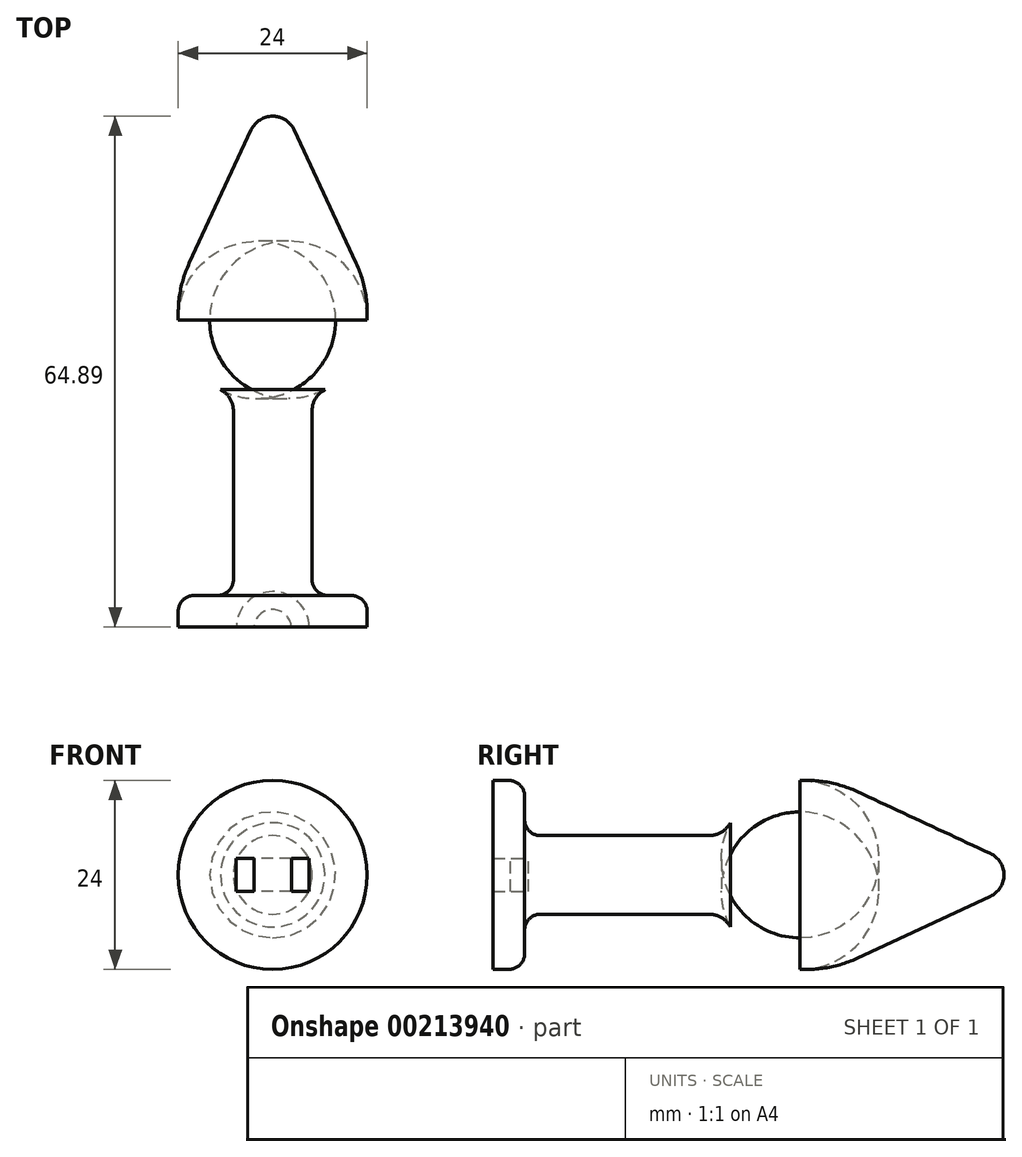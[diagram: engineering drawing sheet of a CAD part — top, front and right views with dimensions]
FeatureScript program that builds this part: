
annotation { "Feature Type Name" : "Feature", "Feature Type Description" : "" }
export const myFeature = defineFeature(function(context is Context, id is Id, definition is map)
    precondition{}
    {
        {
            var Q0;
            Q0=qCreatedBy(makeId("Top.planeOp"),FACE);
            var sketch = newSketch(context, id + "F0", { "sketchPlane" : qUnion([Q0])});
            skLineSegment(sketch, "E0", {"start": v(5, 0) * mm, "end": v(12, 0) * mm});
            skLineSegment(sketch, "E1", {"start": v(-5, 0) * mm, "end": v(-12, 0) * mm});
            skLineSegment(sketch, "E2", {"start": v(44.5, 65) * mm, "end": v(44.5, 25) * mm});
            skLineSegment(sketch, "E3", {"start": v(0, 25) * mm, "end": v(2, 25) * mm});
            skLineSegment(sketch, "E4", {"start": v(12, 35) * mm, "end": v(12, 35.88) * mm});
            skPoint(sketch, "E5.visualSharp", {"position": v(12, 25) * mm});
            skArc(sketch, "E5.filletArc", {"start": v(6.62, 26.13) * mm, "mid": v(10.55, 29.81) * mm, "end": v(12, 35) * mm});
            skLineSegment(sketch, "E6", {"start": v(2.72, 59.15) * mm, "end": v(10.6, 42.2) * mm});
            skPoint(sketch, "E7.visualSharp", {"position": v(12, 39.2) * mm});
            skArc(sketch, "E7.filletArc", {"start": v(12, 35.88) * mm, "mid": v(11.65, 39.12) * mm, "end": v(10.6, 42.2) * mm});
            skLineSegment(sketch, "E8.MirrorCS", {"start": v(-12, 35) * mm, "end": v(-12, 35.88) * mm});
            skLineSegment(sketch, "E9.MirrorCS", {"start": v(0, 25) * mm, "end": v(-2, 25) * mm});
            skArc(sketch, "E10.MirrorCS", {"start": v(-12, 35.88) * mm, "mid": v(-11.65, 39.12) * mm, "end": v(-10.6, 42.2) * mm});
            skPoint(sketch, "E11.MirrorP", {"position": v(-12, 39.2) * mm});
            skPoint(sketch, "E12.MirrorP", {"position": v(-12, 25) * mm});
            skArc(sketch, "E13.MirrorCS", {"start": v(-6.62, 26.13) * mm, "mid": v(-10.55, 29.81) * mm, "end": v(-12, 35) * mm});
            skLineSegment(sketch, "E14.MirrorCS", {"start": v(-2.72, 59.15) * mm, "end": v(-10.6, 42.2) * mm});
            skPoint(sketch, "E15.visualSharp", {"position": v(0, 65) * mm});
            skArc(sketch, "E15.filletArc", {"start": v(2.72, 59.15) * mm, "mid": v(0, 60.89) * mm, "end": v(-2.72, 59.15) * mm});
            skLineSegment(sketch, "E16", {"start": v(5, 0) * mm, "end": v(5, 23.47) * mm});
            skLineSegment(sketch, "E17", {"start": v(-5, 0) * mm, "end": v(-5, 23.47) * mm});
            skArc(sketch, "E18.filletArc", {"start": v(-5, 23.47) * mm, "mid": v(-5.44, 25.02) * mm, "end": v(-6.62, 26.13) * mm});
            skPoint(sketch, "E19.newPointB", {"position": v(2, 25) * mm});
            skArc(sketch, "E19.filletArc", {"start": v(6.62, 26.13) * mm, "mid": v(5.44, 25.02) * mm, "end": v(5, 23.47) * mm});
            skLineSegment(sketch, "E20", {"start": v(-12, 0) * mm, "end": v(-12, -4) * mm});
            skLineSegment(sketch, "E21", {"start": v(-12, -4) * mm, "end": v(-9, -4) * mm});
            skLineSegment(sketch, "E22", {"start": v(12, -4) * mm, "end": v(12, 0) * mm});
            skLineSegment(sketch, "E23", {"start": v(12, -4) * mm, "end": v(9, -4) * mm});
            skLineSegment(sketch, "E24.trimOffspring", {"start": v(9, -4) * mm, "end": v(12, -4) * mm});
            skPoint(sketch, "E25.start.orphan", {"position": v(-9, -9) * mm});
            skPoint(sketch, "E26.end.orphan", {"position": v(9, -9) * mm});
            skLineSegment(sketch, "E27", {"start": v(-9, -4) * mm, "end": v(9, -4) * mm});
            skLineSegment(sketch, "E28", {"start": v(0, -4) * mm, "end": v(0, -16.14) * mm});
            skPoint(sketch, "E28.endSnap0", {"position": v(0, -4) * mm});
            skLineSegment(sketch, "E29", {"start": v(0, 25) * mm, "end": v(0, 17.2) * mm});
            skLineSegment(sketch, "E30", {"start": v(0, -4) * mm, "end": v(0, 60.89) * mm});
            skSolve(sketch);
        }
        {
            var Q0;
            Q0=makeQuery(id+"F0.imprint","IMPRINT",FACE,{"disambiguationData":[TD([[makeQuery(id+"F0.imprint","IMPRINT",EDGE,{"derivedFrom":sQuery(id+"F0.wireOp",EDGE,"E0")}),-1.0]])]});
            var Q1;
            Q1=sQuery(id+"F0.wireOp",EDGE,"E29");
            revolve(context, id + "F1", {"entities" : qUnion([Q0]), "axis" : qUnion([Q1]), "revolveType" : RevolveType.FULL});
        }
        {
            var Q0;
            Q0=makeQuery(id+"F1.opRevolve","SWEPT_EDGE",EDGE,{"disambiguationData":[OSD([sQuery(id+"F0.wireOp",EDGE,"E0"),sQuery(id+"F0.wireOp",EDGE,"E22")])]});
            fillet(context, id + "F2", {"entities" : qUnion([Q0]), "radius" : 2 * mm, "tangentPropagation" : true, "allowEdgeOverflow" : false});
        }
        {
            var Q0;
            Q0=makeQuery(id+"F1.opRevolve","SWEPT_EDGE",EDGE,{"disambiguationData":[OSD([sQuery(id+"F0.wireOp",EDGE,"E0"),sQuery(id+"F0.wireOp",EDGE,"E16")])]});
            fillet(context, id + "F3", {"entities" : qUnion([Q0]), "radius" : 2 * mm, "tangentPropagation" : true, "allowEdgeOverflow" : false});
        }
        {
            var Q0;
            Q0=qCreatedBy(makeId("Top.planeOp"),FACE);
            var sketch = newSketch(context, id + "F4", { "sketchPlane" : qUnion([Q0])});
            skCircle(sketch, "E31", {"center": v(0, -4.16) * mm, "radius": 2.38 * mm});
            skCircle(sketch, "E32", {"center": v(0, -4.16) * mm, "radius": 4.65 * mm});
            skSolve(sketch);
        }
        {
            var Q0;
            Q0=makeQuery(id+"F4.imprint","IMPRINT",FACE,{"disambiguationData":[TD([[makeQuery(id+"F4.imprint","IMPRINT",EDGE,{"derivedFrom":sQuery(id+"F4.wireOp",EDGE,"VUrJy6v7-4TCb-h59M-sBYu-syu1kkNIdrcf")}),-1.0]])]});
            var Q1;
            Q1=makeQuery(id+"F4.imprint","IMPRINT",FACE,{"disambiguationData":[TD([[makeQuery(id+"F4.imprint","IMPRINT",EDGE,{"derivedFrom":sQuery(id+"F4.wireOp",EDGE,"E31")}),-1.0]])]});
            extrude(context, id + "F5", {"entities" : qUnion([Q0, Q1]), "operationType" : NewBodyOperationType.REMOVE, "endBound" : BoundingType.SYMMETRIC, "oppositeDirection" : true, "depth" : 4.2 * mm});
        }
    });
